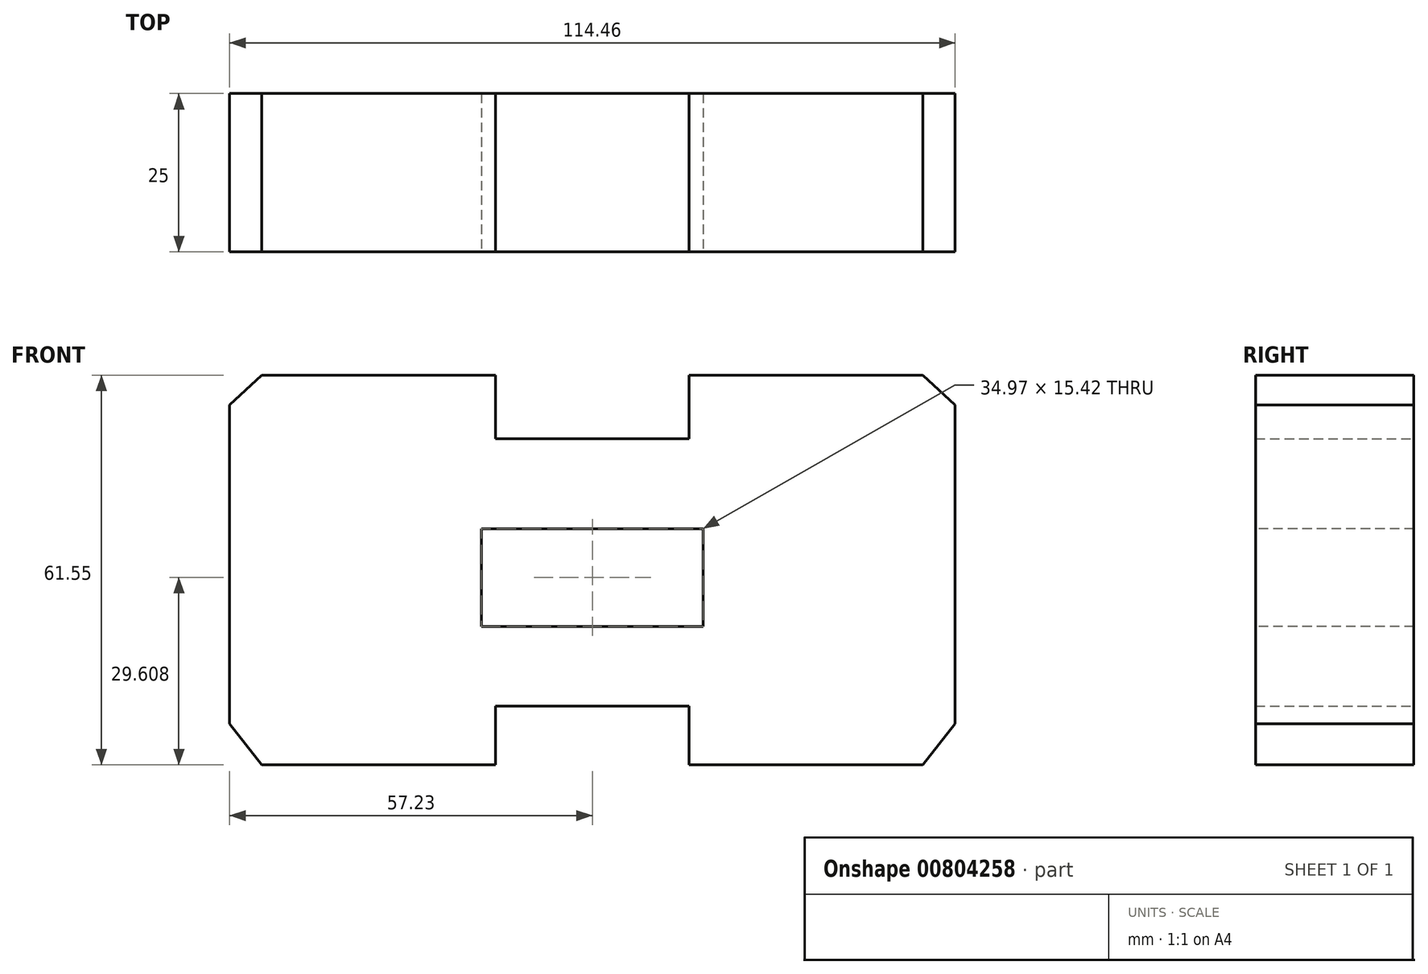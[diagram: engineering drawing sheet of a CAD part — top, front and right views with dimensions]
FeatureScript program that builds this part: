
annotation { "Feature Type Name" : "Feature", "Feature Type Description" : "" }
export const myFeature = defineFeature(function(context is Context, id is Id, definition is map)
    precondition{}
    {
        {
            var Q0;
            Q0=qCreatedBy(makeId("Front.planeOp"),FACE);
            var sketch = newSketch(context, id + "F0", { "sketchPlane" : qUnion([Q0])});
            skLineSegment(sketch, "E0", {"start": v(0, 32.08) * mm, "end": v(0, -31.25) * mm, "construction": true});
            skLineSegment(sketch, "E1", {"start": v(0, 22.05) * mm, "end": v(15.28, 22.05) * mm});
            skLineSegment(sketch, "E2", {"start": v(15.28, 22.05) * mm, "end": v(15.28, 32.08) * mm});
            skLineSegment(sketch, "E3", {"start": v(15.28, 32.08) * mm, "end": v(52.16, 32.08) * mm});
            skLineSegment(sketch, "E4", {"start": v(52.16, 32.08) * mm, "end": v(57.23, 27.4) * mm});
            skLineSegment(sketch, "E5", {"start": v(57.23, 27.4) * mm, "end": v(57.23, 12.76) * mm});
            skLineSegment(sketch, "E6", {"start": v(57.23, 12.76) * mm, "end": v(57.23, -23) * mm});
            skLineSegment(sketch, "E7", {"start": v(57.23, -23) * mm, "end": v(52.16, -29.47) * mm});
            skLineSegment(sketch, "E8", {"start": v(52.16, -29.47) * mm, "end": v(15.28, -29.47) * mm});
            skLineSegment(sketch, "E9", {"start": v(15.28, -29.47) * mm, "end": v(15.28, -20.18) * mm});
            skLineSegment(sketch, "E10", {"start": v(15.28, -20.18) * mm, "end": v(0, -20.18) * mm});
            skLineSegment(sketch, "E11.MirrorCS", {"start": v(0, 22.05) * mm, "end": v(-15.28, 22.05) * mm});
            skLineSegment(sketch, "E12.MirrorCS", {"start": v(-15.28, 22.05) * mm, "end": v(-15.28, 32.08) * mm});
            skLineSegment(sketch, "E13.MirrorCS", {"start": v(-15.28, 32.08) * mm, "end": v(-52.16, 32.08) * mm});
            skLineSegment(sketch, "E14.MirrorCS", {"start": v(-52.16, 32.08) * mm, "end": v(-57.23, 27.4) * mm});
            skLineSegment(sketch, "E15.MirrorCS", {"start": v(-57.23, 27.4) * mm, "end": v(-57.23, 12.76) * mm});
            skLineSegment(sketch, "E16.MirrorCS", {"start": v(-57.23, 12.76) * mm, "end": v(-57.23, -23) * mm});
            skLineSegment(sketch, "E17.MirrorCS", {"start": v(-57.23, -23) * mm, "end": v(-52.16, -29.47) * mm});
            skLineSegment(sketch, "E18.MirrorCS", {"start": v(-52.16, -29.47) * mm, "end": v(-15.28, -29.47) * mm});
            skLineSegment(sketch, "E19.MirrorCS", {"start": v(-15.28, -29.47) * mm, "end": v(-15.28, -20.18) * mm});
            skLineSegment(sketch, "E20.MirrorCS", {"start": v(-15.28, -20.18) * mm, "end": v(0, -20.18) * mm});
            skSolve(sketch);
        }
        {
            var Q0;
            Q0 = qSketchRegion(id + "F0", true);
            extrude(context, id + "F1", {"entities" : qUnion([Q0]), "depth" : 25 * mm, "offsetDistance" : 25 * mm});
        }
        {
            var Q0;
            Q0=makeQuery(id+"F1.opExtrude","CAP_FACE",FACE,{"disambiguationData":[OSD([sQuery(id+"F0.wireOp",EDGE,"E1"),sQuery(id+"F0.wireOp",EDGE,"E2"),sQuery(id+"F0.wireOp",EDGE,"E3"),sQuery(id+"F0.wireOp",EDGE,"E4"),sQuery(id+"F0.wireOp",EDGE,"E5"),sQuery(id+"F0.wireOp",EDGE,"E6"),sQuery(id+"F0.wireOp",EDGE,"E7"),sQuery(id+"F0.wireOp",EDGE,"E8"),sQuery(id+"F0.wireOp",EDGE,"E9"),sQuery(id+"F0.wireOp",EDGE,"E10"),sQuery(id+"F0.wireOp",EDGE,"E11.MirrorCS"),sQuery(id+"F0.wireOp",EDGE,"E12.MirrorCS"),sQuery(id+"F0.wireOp",EDGE,"E13.MirrorCS"),sQuery(id+"F0.wireOp",EDGE,"E14.MirrorCS"),sQuery(id+"F0.wireOp",EDGE,"E15.MirrorCS"),sQuery(id+"F0.wireOp",EDGE,"E16.MirrorCS"),sQuery(id+"F0.wireOp",EDGE,"E17.MirrorCS"),sQuery(id+"F0.wireOp",EDGE,"E18.MirrorCS"),sQuery(id+"F0.wireOp",EDGE,"E19.MirrorCS"),sQuery(id+"F0.wireOp",EDGE,"E20.MirrorCS")])],"isStart":false});
            var sketch = newSketch(context, id + "F2", { "sketchPlane" : qUnion([Q0])});
            skLineSegment(sketch, "E21.bottom", {"start": v(17.48, 7.85) * mm, "end": v(-17.48, 7.85) * mm});
            skLineSegment(sketch, "E21.top", {"start": v(17.48, -7.57) * mm, "end": v(-17.48, -7.57) * mm});
            skLineSegment(sketch, "E21.left", {"start": v(17.48, 7.85) * mm, "end": v(17.48, -7.57) * mm});
            skLineSegment(sketch, "E21.right", {"start": v(-17.48, 7.85) * mm, "end": v(-17.48, -7.57) * mm});
            skSolve(sketch);
        }
        {
            var Q0;
            Q0 = qSketchRegion(id + "F2", true);
            extrude(context, id + "F3", {"entities" : qUnion([Q0]), "operationType" : NewBodyOperationType.REMOVE, "oppositeDirection" : true, "depth" : 25 * mm, "offsetDistance" : 25 * mm});
        }
    });
